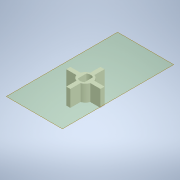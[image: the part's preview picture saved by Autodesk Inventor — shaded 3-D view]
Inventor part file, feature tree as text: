
AUTODESK INVENTOR PART (.ipt)
format: ipt  version: 2022 (Build 260153000, 153)  size: 168,960 bytes
history: native  units: mm
features: extrude x3, sketch x3, other x2, plane x1, projected_geometry x1
ambient origin geometry x8: Origin, YZ Plane, XZ Plane, XY Plane, X Axis, Y Axis, Z Axis, Center Point
bodies: Solid1 (feature_tree)
feature tree (10):
  extrude  "Extrusion1"  Depth=2.0mm
  extrude  "Extrusion2"  Depth=5.0mm TaperAngle=360.0deg
  sketch  "Sketch3"  dims[d7=3.329203mm d8=10.400271mm d9=3.535534mm d10=5.0mm d11=0.0mm d12=5.2mm d13=3.2mm d14=3.0mm d15=0.0mm d16=10.0mm d17=0.0mm]
  plane  "Work Plane1"
  extrude  "Extrusion3"  Depth=10.0mm
  sketch  "Sketch1"  dims[d0=7.0mm d1=2.0mm]
  sketch  "Sketch2"  dims[d2=5.0mm d3=40.0mm d5=360.0deg]
  projected_geometry  "Projected Loop1"
  other  "Assembly2"
  other  "body:1"
